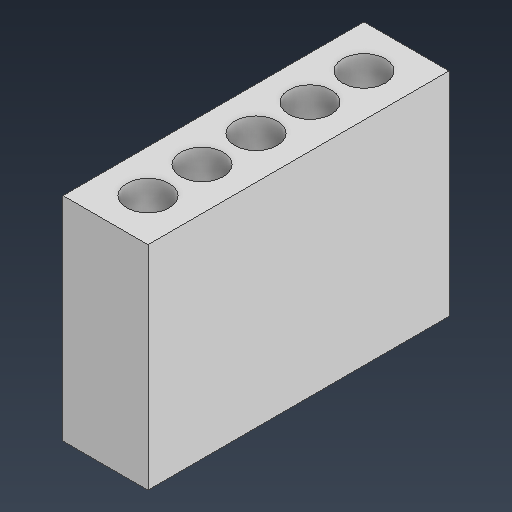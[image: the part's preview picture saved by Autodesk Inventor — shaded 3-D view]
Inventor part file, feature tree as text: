
AUTODESK INVENTOR PART (.ipt)
format: ipt  version: 2025.3 (Build 293356000, 356)  size: 109,056 bytes
history: native  units: mm
features: sketch x2, extrude x1
ambient origin geometry x8: Origin, YZ Plane, XZ Plane, XY Plane, X Axis, Y Axis, Z Axis, Center Point
bodies: Solid1 (feature_tree)
feature tree (3):
  extrude  "Extrusion1"  Depth=2.54mm
  sketch  "Sketch1"  dims[d0=2.0mm d1=50.0mm d3=2.54mm d4=10.0mm d6=10.0mm]
  sketch  "Sketch Rectangular Pattern1"  dims[d8=1.0mm d9=1.0mm d10=1.0mm d11=1.0mm d12=10.0mm d13=0.0mm]
